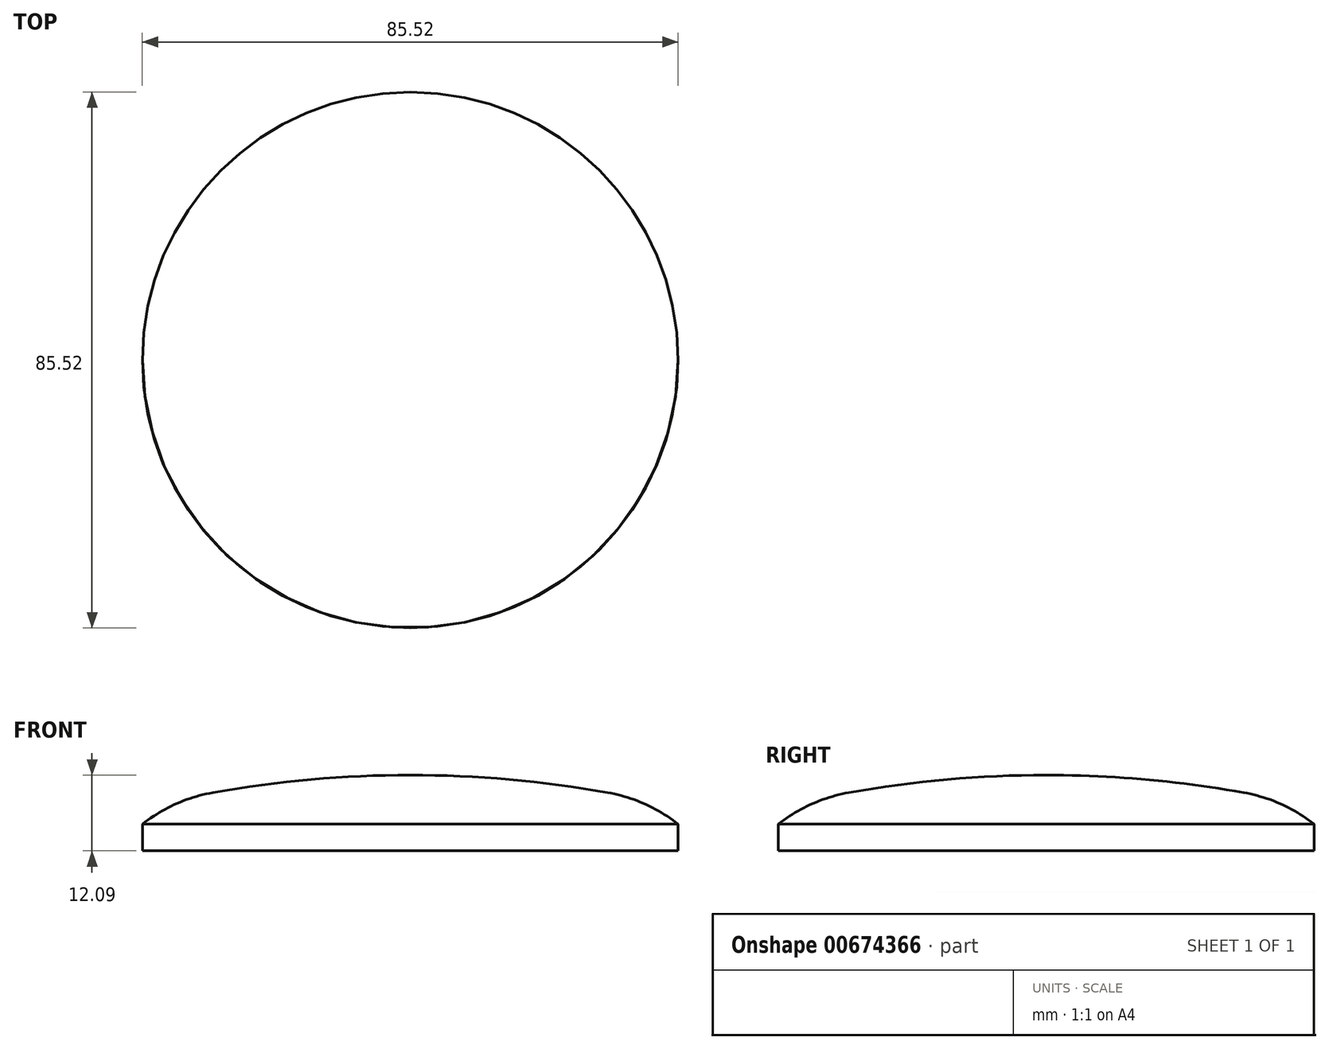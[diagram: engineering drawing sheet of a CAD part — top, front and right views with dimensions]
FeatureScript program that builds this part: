
annotation { "Feature Type Name" : "Feature", "Feature Type Description" : "" }
export const myFeature = defineFeature(function(context is Context, id is Id, definition is map)
    precondition{}
    {
        {
            var Q0;
            Q0=qCreatedBy(makeId("Right.planeOp"),FACE);
            var sketch = newSketch(context, id + "F0", { "sketchPlane" : qUnion([Q0])});
            skLineSegment(sketch, "E0.bottom", {"start": v(0, 0) * mm, "end": v(42.76, 0) * mm});
            skLineSegment(sketch, "E0.top", {"start": v(0, 4.25) * mm, "end": v(42.76, 4.25) * mm});
            skLineSegment(sketch, "E0.left", {"start": v(0, 0) * mm, "end": v(0, 4.25) * mm});
            skLineSegment(sketch, "E0.right", {"start": v(42.76, 0) * mm, "end": v(42.76, 4.25) * mm});
            skLineSegment(sketch, "E1", {"start": v(0, 0) * mm, "end": v(0, 34.68) * mm, "construction": true});
            skSolve(sketch);
        }
        {
            var Q0;
            Q0 = qSketchRegion(id + "F0", true);
            var Q1;
            Q1=sQuery(id+"F0.wireOp",EDGE,"E1");
            revolve(context, id + "F1", {"entities" : qUnion([Q0]), "axis" : qUnion([Q1]), "revolveType" : RevolveType.FULL});
        }
        {
            var Q0;
            Q0=qCreatedBy(makeId("Right.planeOp"),FACE);
            var sketch = newSketch(context, id + "F2", { "sketchPlane" : qUnion([Q0])});
            skLineSegment(sketch, "E2.bottom", {"start": v(42.76, 4.25) * mm, "end": v(0, 4.25) * mm});
            skLineSegment(sketch, "E2.left", {"start": v(42.76, 4.25) * mm, "end": v(42.76, 6.92) * mm});
            skLineSegment(sketch, "E2.right", {"start": v(0, 4.25) * mm, "end": v(0, 12.1) * mm});
            skArc(sketch, "E3", {"start": v(42.76, 6.92) * mm, "mid": v(21.53, 10.8) * mm, "end": v(0, 12.1) * mm});
            skLineSegment(sketch, "E4", {"start": v(0, 12.1) * mm, "end": v(-14.48, 12.1) * mm, "construction": true});
            skSolve(sketch);
        }
        {
            var Q0;
            Q0 = qSketchRegion(id + "F2", true);
            var Q1;
            Q1=sQuery(id+"F2.wireOp",EDGE,"E2.right");
            revolve(context, id + "F3", {"entities" : qUnion([Q0]), "axis" : qUnion([Q1]), "revolveType" : RevolveType.FULL});
        }
        {
            var Q0;
            Q0=makeQuery(id+"F3.opRevolve","SWEPT_EDGE",EDGE,{"disambiguationData":[OSD([sQuery(id+"F2.wireOp",EDGE,"E2.left"),sQuery(id+"F2.wireOp",EDGE,"E3")])]});
            fillet(context, id + "F4", {"entities" : qUnion([Q0]), "radius" : 25.4 * mm, "tangentPropagation" : true, "rho" : 0.5, "crossSection" : FilletCrossSection.CONIC, "allowEdgeOverflow" : false});
        }
    });
